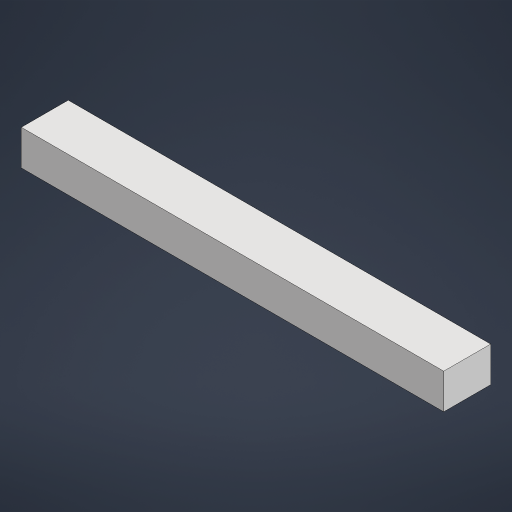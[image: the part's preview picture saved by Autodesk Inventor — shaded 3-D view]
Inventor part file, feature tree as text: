
AUTODESK INVENTOR PART (.ipt)
format: ipt  version: 2023.2 (Build 272271000, 271)  size: 158,720 bytes
history: native  units: in
note: dims shown in document units (in); Inventor stores cm internally (conversion verified against a paired STEP export)
features: extrude x1, sketch x1
ambient origin geometry x8: Origin, YZ Plane, XZ Plane, XY Plane, X Axis, Y Axis, Z Axis, Center Point
bodies: Solid1 (feature_tree)
feature tree (2):
  extrude  "Extrusion1"  Depth=2.0in
  sketch  "Sketch2"  dims[d3=1.5in d4=2.0in d5=18.0in d6=0.0in]
